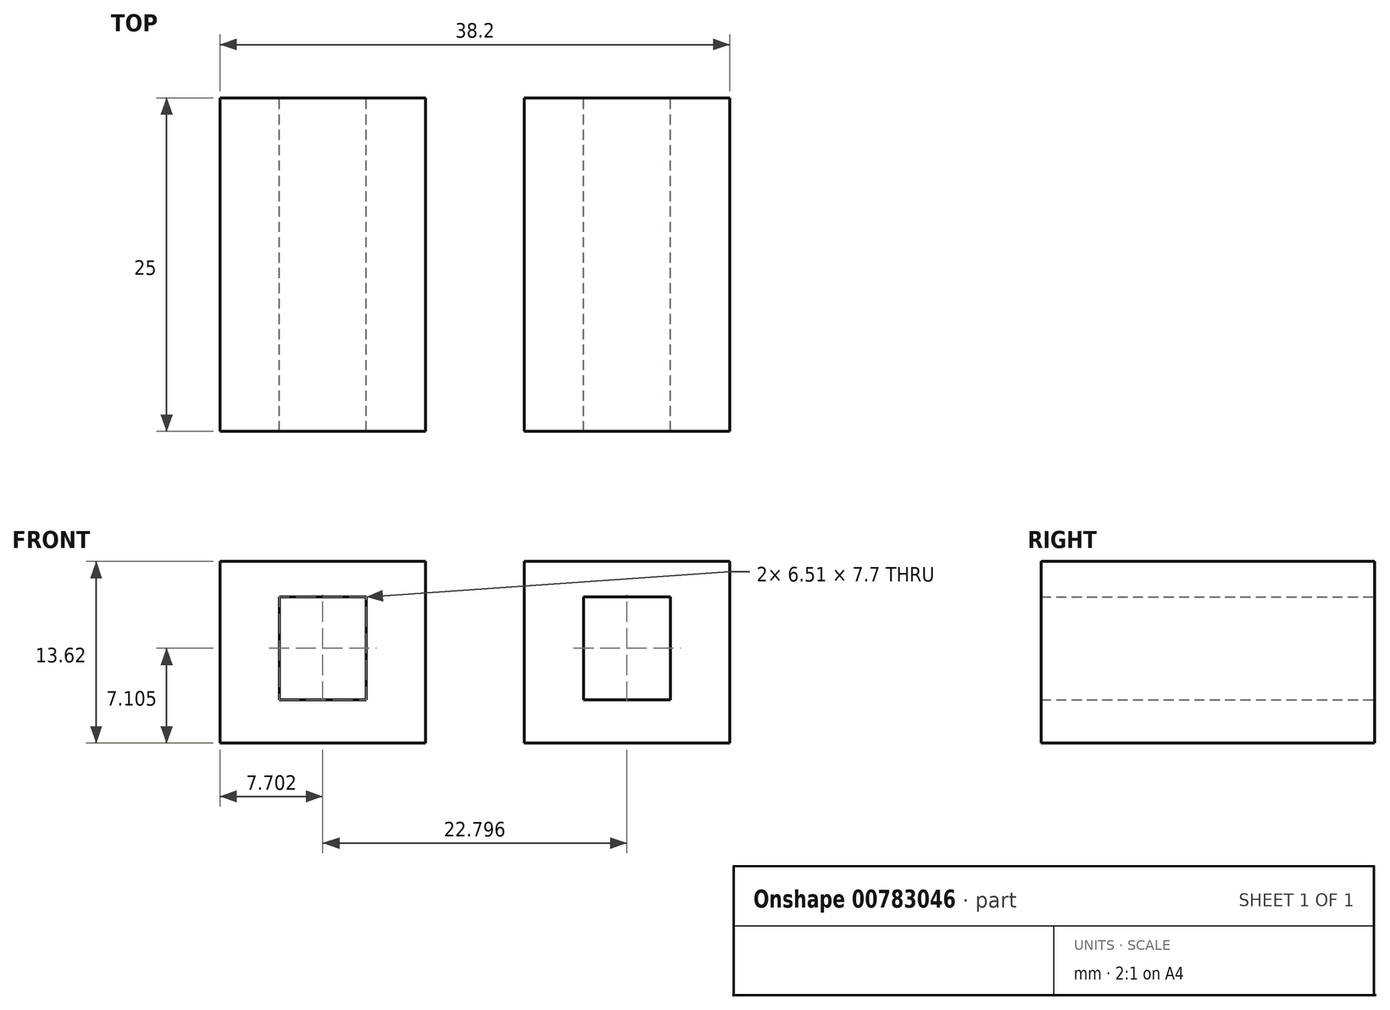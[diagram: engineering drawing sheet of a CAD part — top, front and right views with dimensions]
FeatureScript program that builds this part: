
annotation { "Feature Type Name" : "Feature", "Feature Type Description" : "" }
export const myFeature = defineFeature(function(context is Context, id is Id, definition is map)
    precondition{}
    {
        {
            var Q0;
            Q0=qCreatedBy(makeId("Front.planeOp"),FACE);
            var sketch = newSketch(context, id + "F0", { "sketchPlane" : qUnion([Q0])});
            skLineSegment(sketch, "E0.bottom", {"start": v(-14.65, 34.2) * mm, "end": v(-8.14, 34.2) * mm});
            skLineSegment(sketch, "E0.top", {"start": v(-14.65, 26.5) * mm, "end": v(-8.14, 26.5) * mm});
            skLineSegment(sketch, "E0.left", {"start": v(-14.65, 34.2) * mm, "end": v(-14.65, 26.5) * mm});
            skLineSegment(sketch, "E0.right", {"start": v(-8.14, 34.2) * mm, "end": v(-8.14, 26.5) * mm});
            skLineSegment(sketch, "E1.bottom", {"start": v(-19.1, 36.86) * mm, "end": v(-3.7, 36.86) * mm});
            skLineSegment(sketch, "E1.top", {"start": v(-19.1, 23.24) * mm, "end": v(-3.7, 23.24) * mm});
            skLineSegment(sketch, "E1.left", {"start": v(-19.1, 36.86) * mm, "end": v(-19.1, 23.24) * mm});
            skLineSegment(sketch, "E1.right", {"start": v(-3.7, 36.86) * mm, "end": v(-3.7, 23.24) * mm});
            skLineSegment(sketch, "E2.MirrorCS", {"start": v(19.1, 36.86) * mm, "end": v(3.7, 36.86) * mm});
            skLineSegment(sketch, "E3.MirrorCS", {"start": v(19.1, 36.86) * mm, "end": v(19.1, 23.24) * mm});
            skLineSegment(sketch, "E4.MirrorCS", {"start": v(19.1, 23.24) * mm, "end": v(3.7, 23.24) * mm});
            skLineSegment(sketch, "E5.MirrorCS", {"start": v(3.7, 36.86) * mm, "end": v(3.7, 23.24) * mm});
            skLineSegment(sketch, "E6.MirrorCS", {"start": v(14.65, 34.2) * mm, "end": v(8.14, 34.2) * mm});
            skLineSegment(sketch, "E7.MirrorCS", {"start": v(14.65, 34.2) * mm, "end": v(14.65, 26.5) * mm});
            skLineSegment(sketch, "E8.MirrorCS", {"start": v(14.65, 26.5) * mm, "end": v(8.14, 26.5) * mm});
            skLineSegment(sketch, "E9.MirrorCS", {"start": v(8.14, 34.2) * mm, "end": v(8.14, 26.5) * mm});
            skSolve(sketch);
        }
        {
            var Q0;
            Q0=makeQuery(id+"F0.imprint","IMPRINT",FACE,{"disambiguationData":[TD([[makeQuery(id+"F0.imprint","IMPRINT",EDGE,{"derivedFrom":sQuery(id+"F0.wireOp",EDGE,"E0.bottom")}),1.0]])]});
            var Q1;
            Q1=makeQuery(id+"F0.imprint","IMPRINT",FACE,{"disambiguationData":[TD([[makeQuery(id+"F0.imprint","IMPRINT",EDGE,{"derivedFrom":sQuery(id+"F0.wireOp",EDGE,"E2.MirrorCS")}),1.0]])]});
            extrude(context, id + "F1", {"entities" : qUnion([Q0, Q1]), "depth" : 25 * mm, "offsetDistance" : 25 * mm});
        }
    });
